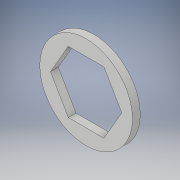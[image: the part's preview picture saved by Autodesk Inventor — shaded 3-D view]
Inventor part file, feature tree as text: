
AUTODESK INVENTOR PART (.ipt)
format: ipt  version: 2018 (Build 220112000, 112)  size: 102,912 bytes
history: native  units: in
note: dims shown in document units (in); Inventor stores cm internally (conversion verified against a paired STEP export)
features: extrude x1, sketch x1
ambient origin geometry x8: Origin, YZ Plane, XZ Plane, XY Plane, X Axis, Y Axis, Z Axis, Center Point
bodies: Solid1 (feature_tree)
feature tree (2):
  extrude  "Extrusion1"  Depth=0.0625in
  sketch  "Sketch1"  dims[d0=0.5in d1=0.75in d2=0.0625in d3=0.0in]
